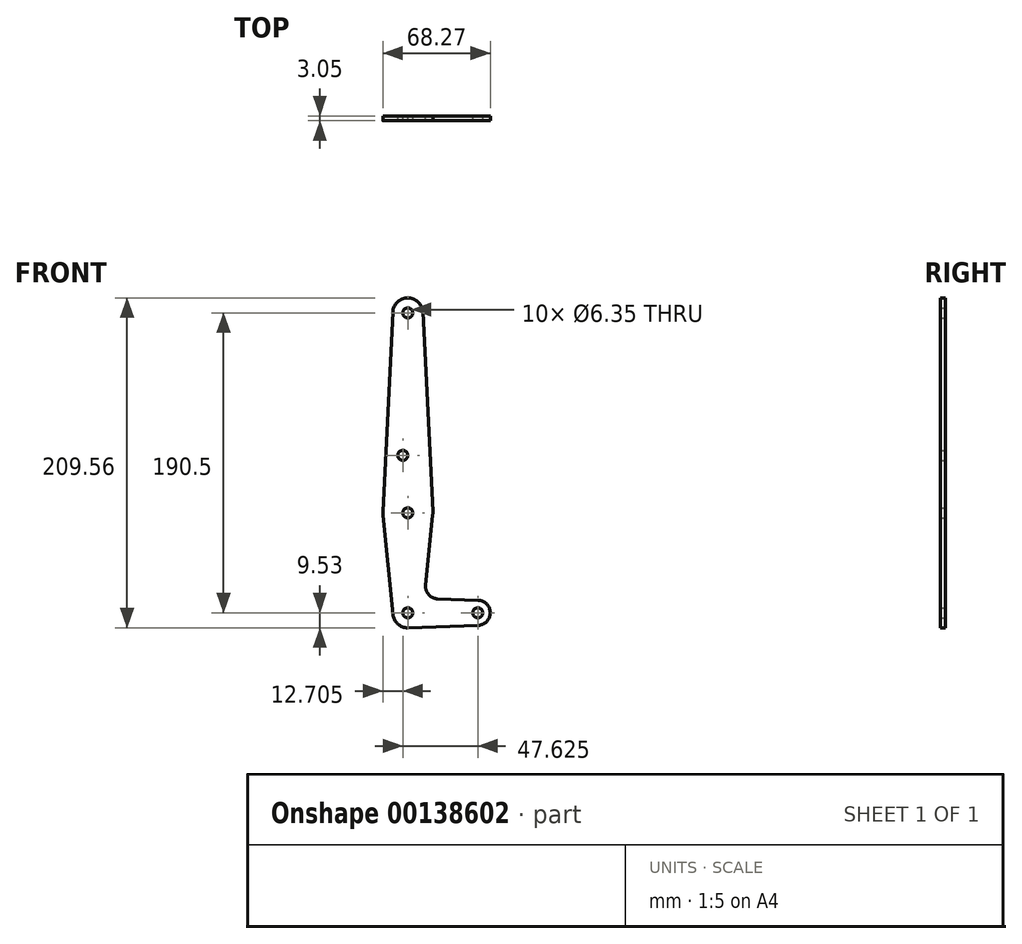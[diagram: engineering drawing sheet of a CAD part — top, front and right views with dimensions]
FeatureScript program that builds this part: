
annotation { "Feature Type Name" : "Feature", "Feature Type Description" : "" }
export const myFeature = defineFeature(function(context is Context, id is Id, definition is map)
    precondition{}
    {
        {
            var Q0;
            Q0=qCreatedBy(makeId("Front.planeOp"),FACE);
            var sketch = newSketch(context, id + "F0", { "sketchPlane" : qUnion([Q0])});
            skCircle(sketch, "E0", {"center": v(0, 0) * mm, "radius": 9.53 * mm});
            skCircle(sketch, "E1", {"center": v(0, 63.5) * mm, "radius": 15.88 * mm});
            skCircle(sketch, "E2", {"center": v(0, 190.5) * mm, "radius": 9.53 * mm});
            skCircle(sketch, "E3", {"center": v(44.45, 0) * mm, "radius": 7.94 * mm});
            skLineSegment(sketch, "E4", {"start": v(0, 190.5) * mm, "end": v(0, 0) * mm, "construction": true});
            skLineSegment(sketch, "E5", {"start": v(44.45, 0) * mm, "end": v(0, 0) * mm, "construction": true});
            skLineSegment(sketch, "E6", {"start": v(-15.86, 64.3) * mm, "end": v(-9.51, 190.98) * mm});
            skLineSegment(sketch, "E7", {"start": v(15.86, 64.3) * mm, "end": v(9.51, 190.98) * mm});
            skLineSegment(sketch, "E8", {"start": v(15.8, 61.91) * mm, "end": v(11.34, 17.6) * mm});
            skLineSegment(sketch, "E9", {"start": v(0, -9.53) * mm, "end": v(44.73, -7.93) * mm});
            skCircle(sketch, "E10", {"center": v(-3.17, 100.03) * mm, "radius": 3.18 * mm});
            skCircle(sketch, "E11", {"center": v(0, 63.5) * mm, "radius": 3.18 * mm});
            skCircle(sketch, "E12", {"center": v(0, 0) * mm, "radius": 3.18 * mm});
            skCircle(sketch, "E13", {"center": v(44.45, 0) * mm, "radius": 3.18 * mm});
            skCircle(sketch, "E14", {"center": v(0, 190.5) * mm, "radius": 3.18 * mm});
            skLineSegment(sketch, "E15", {"start": v(18.97, 8.85) * mm, "end": v(44.73, 7.93) * mm});
            skArc(sketch, "E16.filletArc", {"start": v(11.34, 17.6) * mm, "mid": v(13.26, 11.57) * mm, "end": v(18.97, 8.85) * mm});
            skLineSegment(sketch, "E17", {"start": v(-15.8, 61.91) * mm, "end": v(-9.48, -0.95) * mm});
            skSolve(sketch);
        }
        {
            var Q0;
            {var subQ1=sQuery(id+"F0.wireOp",EDGE,"E6");Q0=makeQuery(id+"F0.imprint","IMPRINT",FACE,{"disambiguationData":[TD([[makeQuery(id+"F0.imprint","IMPRINT",EDGE,{"derivedFrom":subQ1}),-1.0]])]});}
            var Q1;
            {var subQ0=sQuery(id+"F0.wireOp",EDGE,"E8");Q1=makeQuery(id+"F0.imprint","IMPRINT",FACE,{"disambiguationData":[TD([[makeQuery(id+"F0.imprint","IMPRINT",EDGE,{"derivedFrom":subQ0}),-1.0]])]});}
            var Q2;
            Q2=makeQuery(id+"F0.imprint","IMPRINT",FACE,{"disambiguationData":[TD([[makeQuery(id+"F0.imprint","IMPRINT",EDGE,{"derivedFrom":sQuery(id+"F0.wireOp",EDGE,"E11")}),-1.0]])]});
            var Q3;
            Q3=makeQuery(id+"F0.imprint","IMPRINT",FACE,{"disambiguationData":[TD([[makeQuery(id+"F0.imprint","IMPRINT",EDGE,{"derivedFrom":sQuery(id+"F0.wireOp",EDGE,"E12")}),-1.0]])]});
            var Q4;
            Q4=makeQuery(id+"F0.imprint","IMPRINT",FACE,{"disambiguationData":[TD([[makeQuery(id+"F0.imprint","IMPRINT",EDGE,{"derivedFrom":sQuery(id+"F0.wireOp",EDGE,"E13")}),-1.0]])]});
            var Q5;
            Q5=makeQuery(id+"F0.imprint","IMPRINT",FACE,{"disambiguationData":[TD([[makeQuery(id+"F0.imprint","IMPRINT",EDGE,{"derivedFrom":sQuery(id+"F0.wireOp",EDGE,"E14")}),-1.0]])]});
            extrude(context, id + "F1", {"entities" : qUnion([Q0, Q1, Q2, Q3, Q4, Q5]), "depth" : 3.05 * mm});
        }
    });
